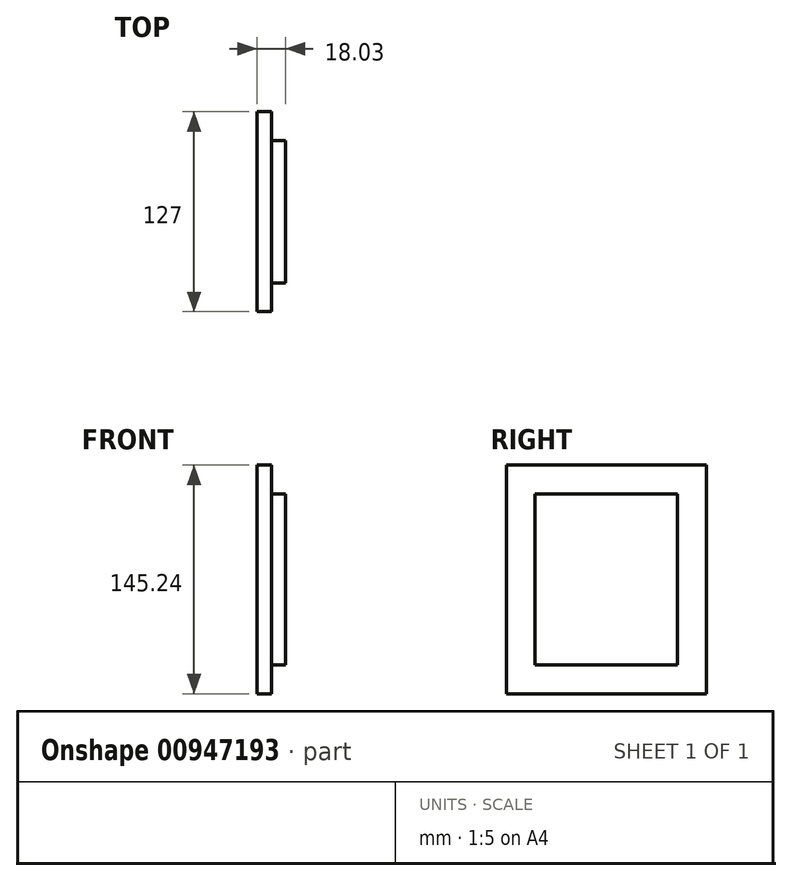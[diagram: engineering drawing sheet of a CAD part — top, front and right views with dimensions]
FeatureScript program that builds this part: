
annotation { "Feature Type Name" : "Feature", "Feature Type Description" : "" }
export const myFeature = defineFeature(function(context is Context, id is Id, definition is map)
    precondition{}
    {
        {
            var Q0;
            Q0=qCreatedBy(makeId("Right.planeOp"),FACE);
            var sketch = newSketch(context, id + "F0", { "sketchPlane" : qUnion([Q0])});
            skLineSegment(sketch, "E0.bottom", {"start": v(0, 0) * mm, "end": v(127, 0) * mm});
            skLineSegment(sketch, "E0.top", {"start": v(0, 145.24) * mm, "end": v(127, 145.24) * mm});
            skLineSegment(sketch, "E0.left", {"start": v(0, 0) * mm, "end": v(0, 145.24) * mm});
            skLineSegment(sketch, "E0.right", {"start": v(127, 0) * mm, "end": v(127, 145.24) * mm});
            skSolve(sketch);
        }
        {
            var Q0;
            Q0 = qSketchRegion(id + "F0", true);
            extrude(context, id + "F1", {"entities" : qUnion([Q0]), "depth" : 18.03 * mm, "offsetDistance" : 25.4 * mm});
        }
        {
            var Q0;
            Q0=makeQuery(id+"F1.opExtrude","CAP_FACE",FACE,{"disambiguationData":[OSD([sQuery(id+"F0.wireOp",EDGE,"E0.bottom"),sQuery(id+"F0.wireOp",EDGE,"E0.top"),sQuery(id+"F0.wireOp",EDGE,"E0.left"),sQuery(id+"F0.wireOp",EDGE,"E0.right")])],"isStart":false});
            var sketch = newSketch(context, id + "F2", { "sketchPlane" : qUnion([Q0])});
            skLineSegment(sketch, "E1.0", {"start": v(18.22, 127.01) * mm, "end": v(108.78, 127.01) * mm});
            skLineSegment(sketch, "E1.1", {"start": v(18.22, 18.22) * mm, "end": v(18.22, 127.01) * mm});
            skLineSegment(sketch, "E1.2", {"start": v(18.22, 18.22) * mm, "end": v(108.78, 18.22) * mm});
            skLineSegment(sketch, "E1.3", {"start": v(108.78, 18.22) * mm, "end": v(108.78, 127.01) * mm});
            skLineSegment(sketch, "E2.0", {"start": v(0, 0) * mm, "end": v(0, 145.24) * mm});
            skLineSegment(sketch, "E2.1", {"start": v(0, 145.24) * mm, "end": v(127, 145.24) * mm});
            skLineSegment(sketch, "E2.2", {"start": v(127, 0) * mm, "end": v(127, 145.24) * mm});
            skLineSegment(sketch, "E2.3", {"start": v(0, 0) * mm, "end": v(127, 0) * mm});
            skSolve(sketch);
        }
        {
            var Q0;
            Q0=makeQuery(id+"F2.imprint","IMPRINT",FACE,{"disambiguationData":[TD([[makeQuery(id+"F2.imprint","IMPRINT",EDGE,{"derivedFrom":sQuery(id+"F2.wireOp",EDGE,"E1.0")}),1.0]])]});
            extrude(context, id + "F3", {"entities" : qUnion([Q0]), "operationType" : NewBodyOperationType.REMOVE, "oppositeDirection" : true, "depth" : 9.02 * mm, "offsetDistance" : 25.4 * mm});
        }
    });
